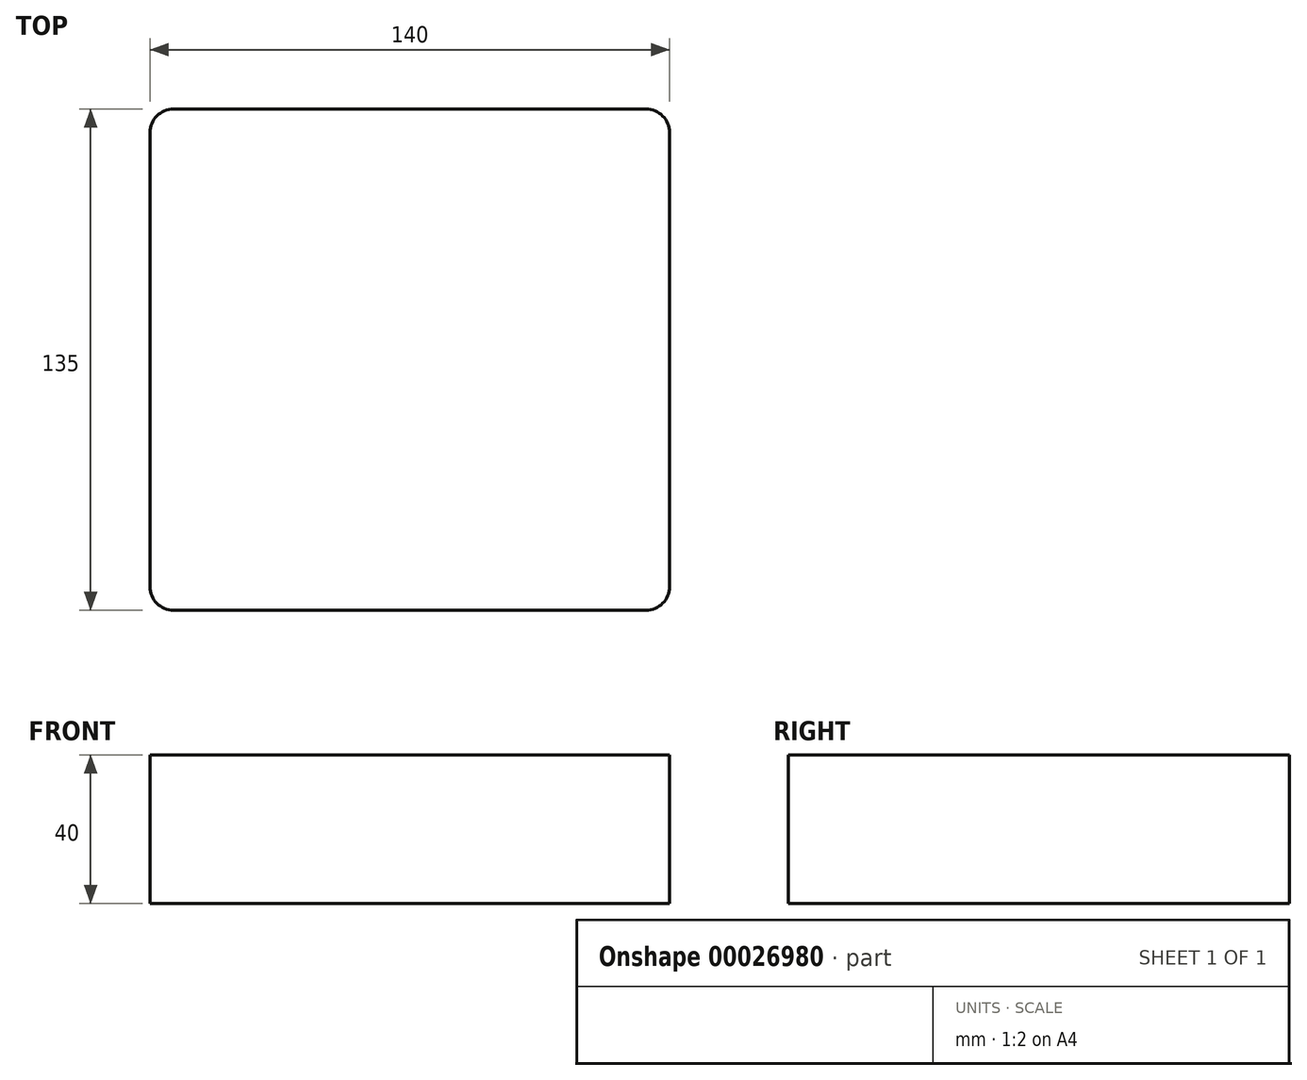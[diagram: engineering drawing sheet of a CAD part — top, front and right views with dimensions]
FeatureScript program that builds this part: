
annotation { "Feature Type Name" : "Feature", "Feature Type Description" : "" }
export const myFeature = defineFeature(function(context is Context, id is Id, definition is map)
    precondition{}
    {
        {
            var Q0;
            Q0=qCreatedBy(makeId("Top.planeOp"),FACE);
            var sketch = newSketch(context, id + "F0", { "sketchPlane" : qUnion([Q0])});
            skLineSegment(sketch, "E0.rect.bottom", {"start": v(-70, -67.5) * mm, "end": v(70, -67.5) * mm});
            skLineSegment(sketch, "E0.rect.top", {"start": v(-70, 67.5) * mm, "end": v(70, 67.5) * mm});
            skLineSegment(sketch, "E0.rect.left", {"start": v(-70, -67.5) * mm, "end": v(-70, 67.5) * mm});
            skLineSegment(sketch, "E0.rect.right", {"start": v(70, -67.5) * mm, "end": v(70, 67.5) * mm});
            skPoint(sketch, "E0.rect.middle", {"position": v(0, 0) * mm});
            skSolve(sketch);
        }
        {
            var Q0;
            Q0=makeQuery(id+"F0.imprint","IMPRINT",FACE,{"disambiguationData":[TD([[makeQuery(id+"F0.imprint","IMPRINT",EDGE,{"derivedFrom":sQuery(id+"F0.wireOp",EDGE,"E0.rect.bottom")}),1.0]])]});
            extrude(context, id + "F1", {"entities" : qUnion([Q0]), "depth" : 40 * mm});
        }
        {
            var Q0;
            Q0=makeQuery(id+"F1.opExtrude","SWEPT_EDGE",EDGE,{"disambiguationData":[OSD([sQuery(id+"F0.wireOp",EDGE,"E0.rect.bottom"),sQuery(id+"F0.wireOp",EDGE,"E0.rect.left")])]});
            var Q1;
            Q1=makeQuery(id+"F1.opExtrude","SWEPT_EDGE",EDGE,{"disambiguationData":[OSD([sQuery(id+"F0.wireOp",EDGE,"E0.rect.bottom"),sQuery(id+"F0.wireOp",EDGE,"E0.rect.right")])]});
            var Q2;
            Q2=makeQuery(id+"F1.opExtrude","SWEPT_EDGE",EDGE,{"disambiguationData":[OSD([sQuery(id+"F0.wireOp",EDGE,"E0.rect.top"),sQuery(id+"F0.wireOp",EDGE,"E0.rect.right")])]});
            var Q3;
            Q3=makeQuery(id+"F1.opExtrude","SWEPT_EDGE",EDGE,{"disambiguationData":[OSD([sQuery(id+"F0.wireOp",EDGE,"E0.rect.top"),sQuery(id+"F0.wireOp",EDGE,"E0.rect.left")])]});
            fillet(context, id + "F2", {"entities" : qUnion([Q0, Q1, Q2, Q3]), "radius" : 6.35 * mm, "tangentPropagation" : true, "allowEdgeOverflow" : false});
        }
    });
